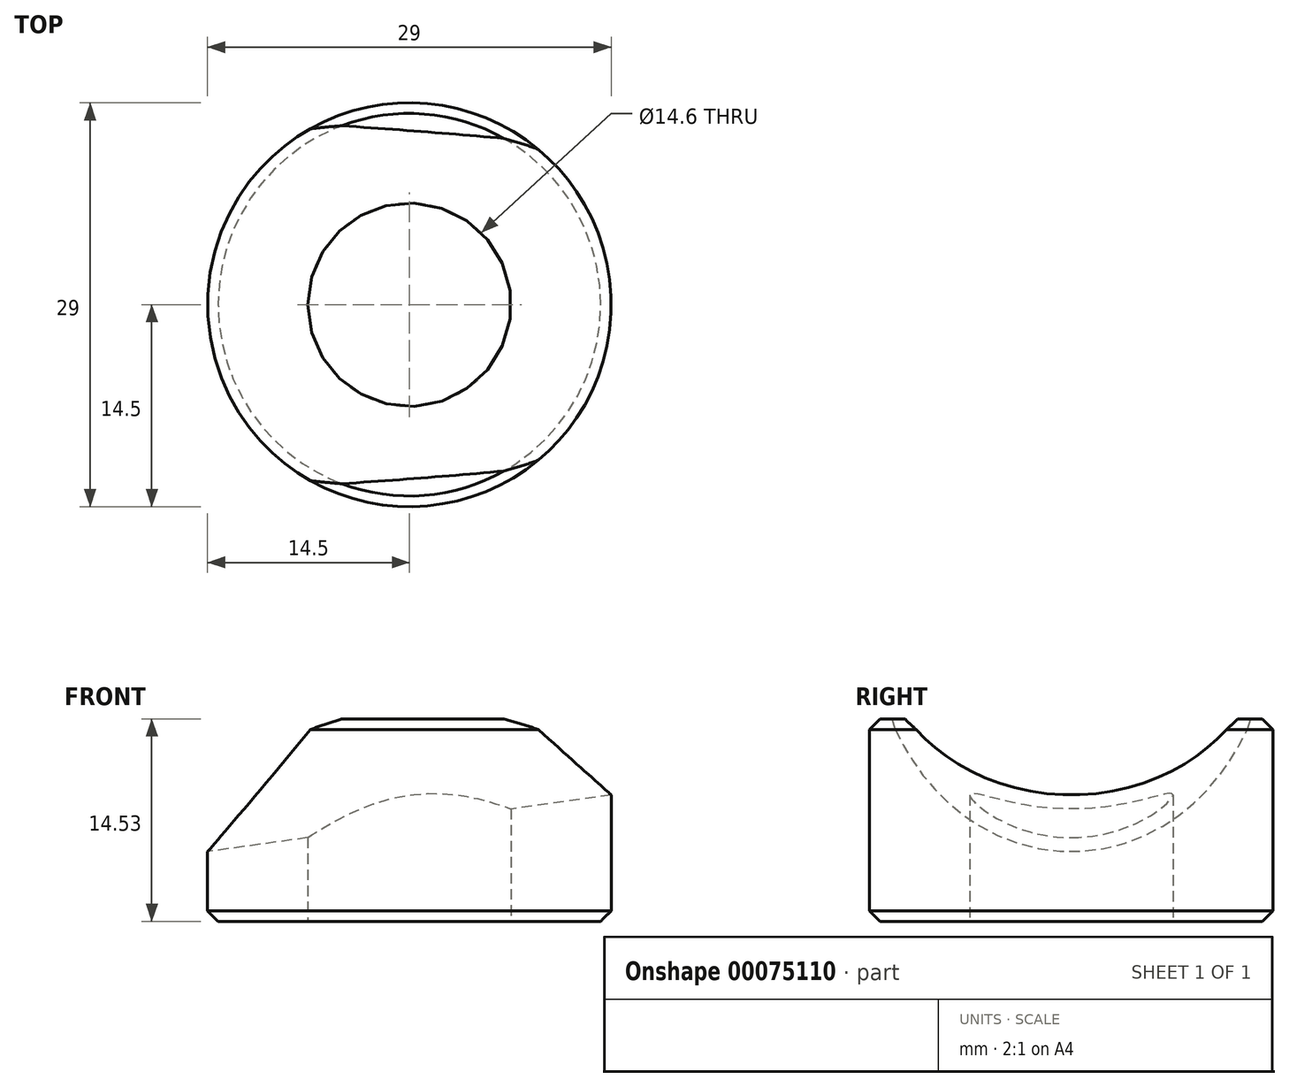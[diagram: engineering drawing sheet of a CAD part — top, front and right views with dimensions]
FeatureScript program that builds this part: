
annotation { "Feature Type Name" : "Feature", "Feature Type Description" : "" }
export const myFeature = defineFeature(function(context is Context, id is Id, definition is map)
    precondition{}
    {
        {
            var Q0;
            Q0=qCreatedBy(makeId("Top.planeOp"),FACE);
            var sketch = newSketch(context, id + "F0", { "sketchPlane" : qUnion([Q0])});
            skCircle(sketch, "E0", {"center": v(0, 0) * mm, "radius": 14.5 * mm});
            skCircle(sketch, "E1", {"center": v(0, 0) * mm, "radius": 7.3 * mm});
            skSolve(sketch);
        }
        {
            var Q0;
            Q0=makeQuery(id+"F0.imprint","IMPRINT",FACE,{"disambiguationData":[TD([[makeQuery(id+"F0.imprint","IMPRINT",EDGE,{"derivedFrom":sQuery(id+"F0.wireOp",EDGE,"E0")}),1.0]])]});
            extrude(context, id + "F1", {"entities" : qUnion([Q0]), "depth" : 14.53 * mm});
        }
        {
            var Q0;
            Q0=qCreatedBy(makeId("Front.planeOp"),FACE);
            var sketch = newSketch(context, id + "F2", { "sketchPlane" : qUnion([Q0])});
            skLineSegment(sketch, "E2", {"start": v(-12.73, -7.58) * mm, "end": v(-16.27, 17.58) * mm, "construction": true});
            skLineSegment(sketch, "E3", {"start": v(-14.5, 5) * mm, "end": v(-50.08, 0) * mm, "construction": true});
            skLineSegment(sketch, "E4.0", {"start": v(-14.5, 0) * mm, "end": v(14.5, 0) * mm, "construction": true});
            skLineSegment(sketch, "E5", {"start": v(-14.5, 0) * mm, "end": v(-14.5, 14.53) * mm, "construction": true});
            skSolve(sketch);
        }
        {
            var Q0;
            Q0=sQuery(id+"F2.wireOp",VERTEX,"E3.start");
            var Q1;
            Q1=sQuery(id+"F2.wireOp",EDGE,"E3");
            cPlane(context, id + "F3", {"entities" : qUnion([Q0, Q1]), "cplaneType" : CPlaneType.LINE_POINT, "offset" : 152.4 * mm, "width" : 152.4 * mm, "height" : 152.4 * mm});
        }
        {
            var Q0;
            Q0=makeQuery(id+"F1.opExtrude","CAP_EDGE",EDGE,{"disambiguationData":[OSD([sQuery(id+"F0.wireOp",EDGE,"E0")])],"isStart":false});
            var Q1;
            Q1=makeQuery(id+"F1.opExtrude","CAP_EDGE",EDGE,{"disambiguationData":[OSD([sQuery(id+"F0.wireOp",EDGE,"E0")])],"isStart":true});
            chamfer(context, id + "F4", {"entities" : qUnion([Q0, Q1]), "width" : 0.76 * mm, "tangentPropagation" : true});
        }
        {
            var Q0;
            Q0=qCreatedBy(id+"F3.planeOp",FACE);
            var sketch = newSketch(context, id + "F5", { "sketchPlane" : qUnion([Q0])});
            skCircle(sketch, "E6", {"center": v(0, 21.22) * mm, "radius": 14.25 * mm});
            skSolve(sketch);
        }
        {
            var Q0;
            Q0=makeQuery(id+"F5.imprint","IMPRINT",FACE,{"disambiguationData":[TD([[makeQuery(id+"F5.imprint","IMPRINT",EDGE,{"derivedFrom":sQuery(id+"F5.wireOp",EDGE,"E6")}),1.0]])]});
            extrude(context, id + "F6", {"entities" : qUnion([Q0]), "operationType" : NewBodyOperationType.REMOVE, "oppositeDirection" : true, "depth" : 127 * mm, "symmetric" : true});
        }
    });
